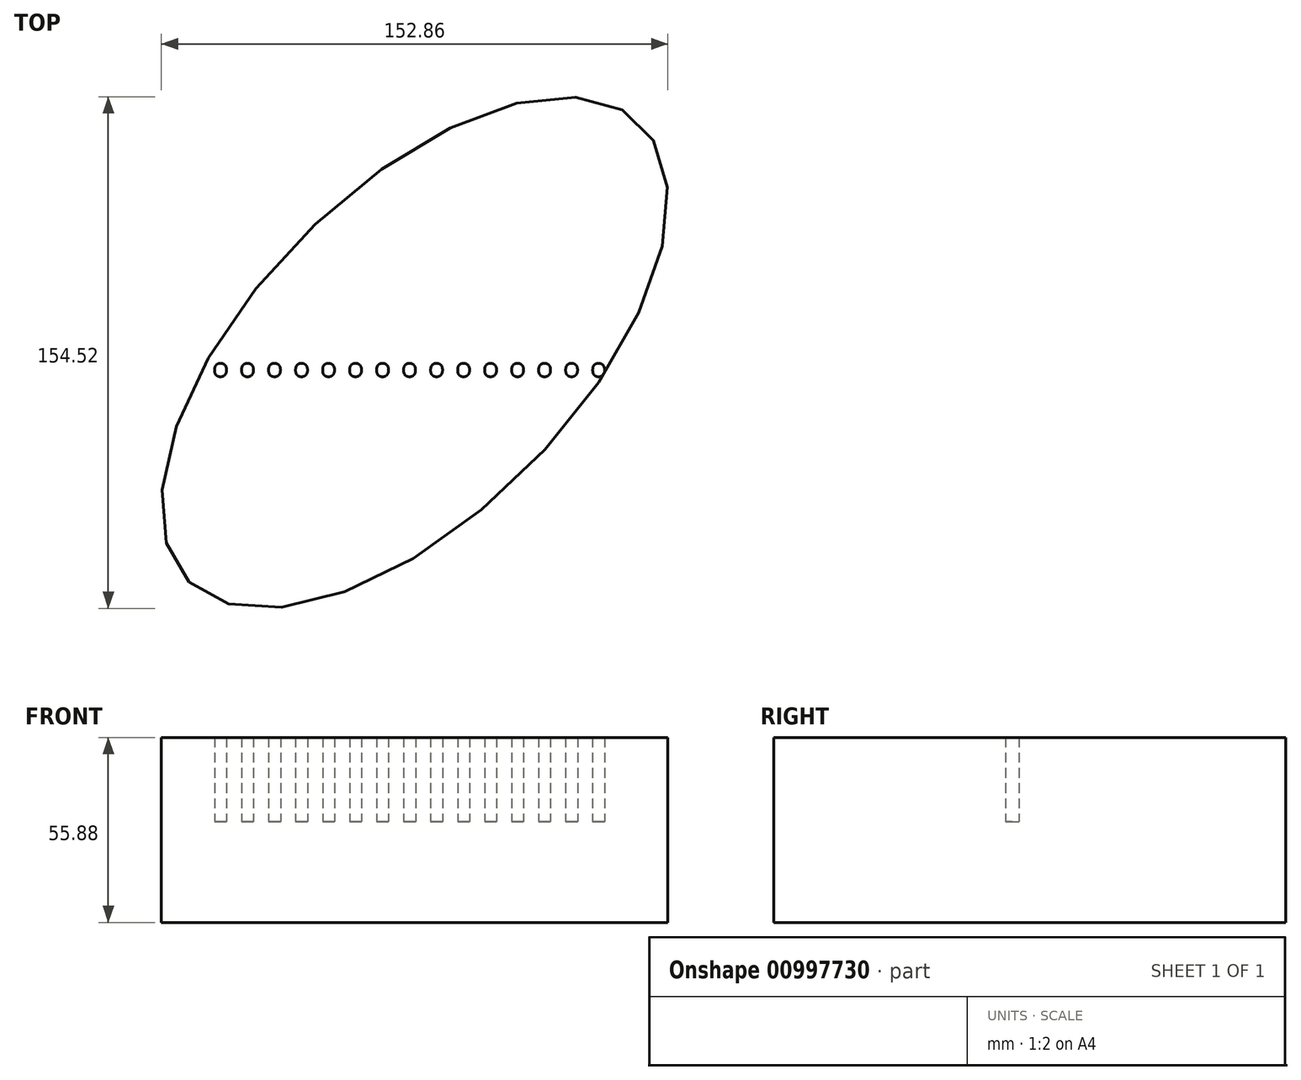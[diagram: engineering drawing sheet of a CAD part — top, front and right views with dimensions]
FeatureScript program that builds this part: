
annotation { "Feature Type Name" : "Feature", "Feature Type Description" : "" }
export const myFeature = defineFeature(function(context is Context, id is Id, definition is map)
    precondition{}
    {
        {
            var Q0;
            Q0=qCreatedBy(makeId("Top.planeOp"),FACE);
            var sketch = newSketch(context, id + "F0", { "sketchPlane" : qUnion([Q0])});
            skEllipse(sketch, "E0", {"center": v(0, 0) * mm, "majorRadius": 81.5 * mm, "minorRadius": 2.55 * mm, "majorAxis": v(-0.72, -0.7)});
            skSolve(sketch);
        }
        {
            var Q0;
            Q0=makeQuery(id+"F0.imprint","IMPRINT",FACE,{"disambiguationData":[TD([[makeQuery(id+"F0.imprint","IMPRINT",EDGE,{"derivedFrom":sQuery(id+"F0.wireOp",EDGE,"E0")}),1.0]])]});
            extrude(context, id + "F1", {"entities" : qUnion([Q0]), "depth" : 37.34 * mm, "offsetDistance" : 25.4 * mm});
        }
        {
            var Q0;
            Q0=qCreatedBy(makeId("Right.planeOp"),FACE);
            var sketch = newSketch(context, id + "F2", { "sketchPlane" : qUnion([Q0])});
            skEllipse(sketch, "E1", {"center": v(0, 0) * mm, "majorRadius": 62.58 * mm, "minorRadius": 22.86 * mm, "majorAxis": v(0.87, 0.5)});
            skSolve(sketch);
        }
        {
            var Q0;
            Q0=makeQuery(id+"F2.imprint","IMPRINT",FACE,{"disambiguationData":[TD([[makeQuery(id+"F2.imprint","IMPRINT",EDGE,{"derivedFrom":sQuery(id+"F2.wireOp",EDGE,"E1")}),1.0]])]});
            extrude(context, id + "F3", {"entities" : qUnion([Q0]), "operationType" : NewBodyOperationType.ADD, "oppositeDirection" : true, "depth" : 25.4 * mm, "offsetDistance" : 25.4 * mm});
        }
        {
            var Q0;
            Q0=makeQuery(id+"F1.opExtrude","SWEPT_BODY",BODY,{"disambiguationData":[OSD([sQuery(id+"F0.wireOp",EDGE,"E0")])]});
            deleteBodies(context, id + "F4", {"entities" : qUnion([Q0])});
        }
        {
            var Q0;
            Q0=qCreatedBy(makeId("Top.planeOp"),FACE);
            var sketch = newSketch(context, id + "F5", { "sketchPlane" : qUnion([Q0])});
            skEllipse(sketch, "E2", {"center": v(0, 0) * mm, "majorRadius": 97.14 * mm, "minorRadius": 48.74 * mm, "majorAxis": v(-0.7, -0.71)});
            skSolve(sketch);
        }
        {
            var Q0;
            Q0 = qSketchRegion(id + "F5", true);
            extrude(context, id + "F6", {"entities" : qUnion([Q0]), "depth" : 30.48 * mm, "offsetDistance" : 25.4 * mm});
        }
        {
            var Q0;
            Q0=makeQuery(id+"F6.opExtrude","CAP_FACE",FACE,{"disambiguationData":[OSD([sQuery(id+"F5.wireOp",EDGE,"E2")])],"isStart":false});
            var sketch = newSketch(context, id + "F7", { "sketchPlane" : qUnion([Q0])});
            skText(sketch, "E3", { "text": "................\n", "fontName": "OpenSans-Regular.ttf"});
            const initialGuessF7  = {"E3": [-0.06265, -0.00687, 1, 0, 0.02206]};
            skSetInitialGuess(sketch, initialGuessF7);
            skSolve(sketch);
        }
        {
            var Q0;
            Q0=makeQuery(id+"F7.imprint","IMPRINT",FACE,{"disambiguationData":[TD([[makeQuery(id+"F7.imprint","IMPRINT",EDGE,{"derivedFrom":sQuery(id+"F7.wireOp",EDGE,"E3.sketch_text.stroke-0")}),1.0]])]});
            extrude(context, id + "F8", {"entities" : qUnion([Q0]), "operationType" : NewBodyOperationType.ADD, "depth" : 25.4 * mm, "offsetDistance" : 25.4 * mm});
        }
    });
